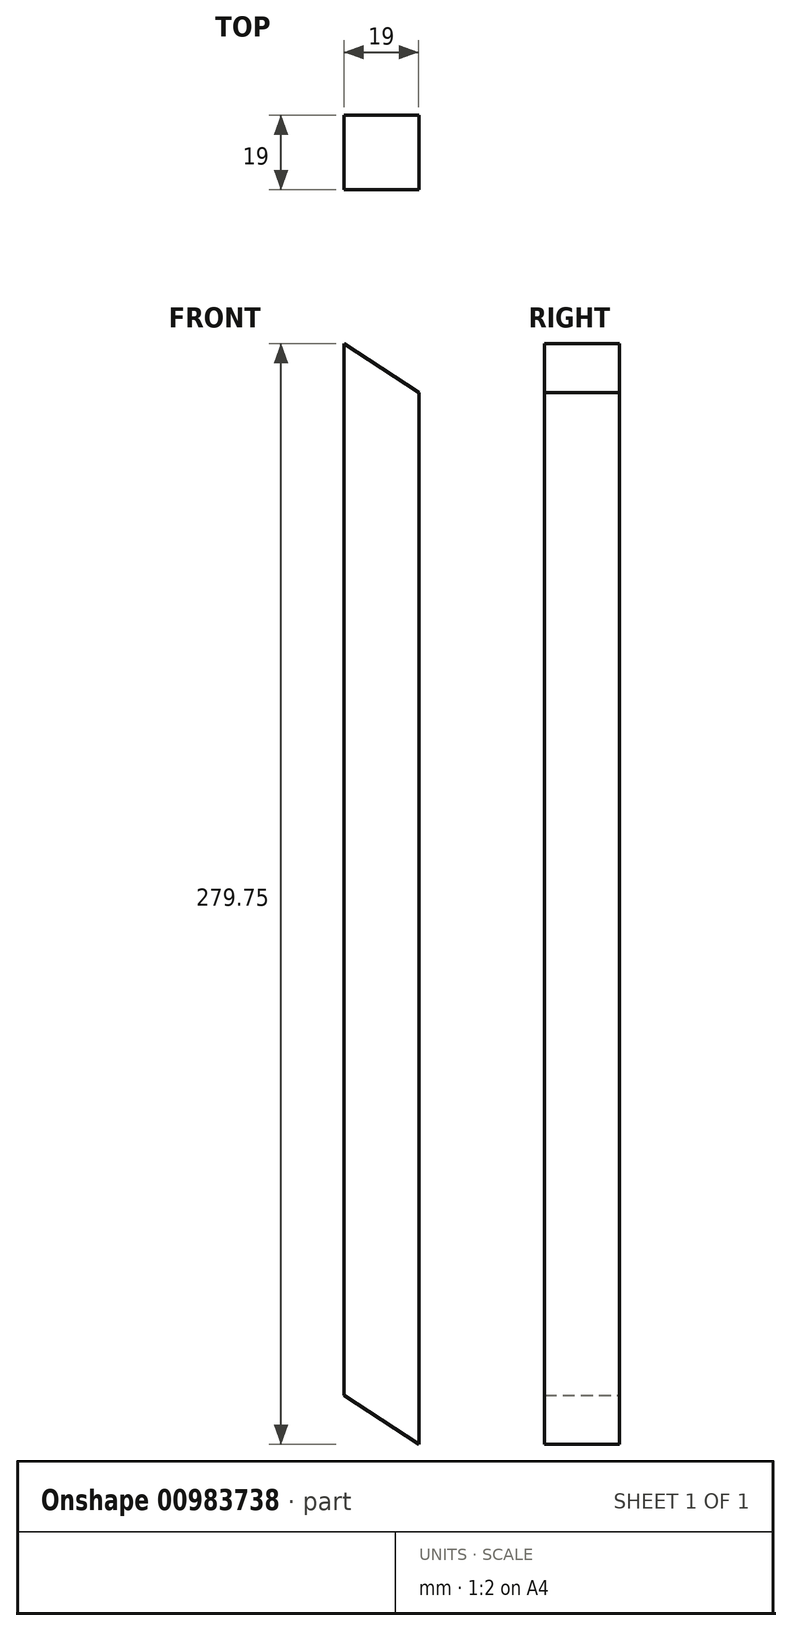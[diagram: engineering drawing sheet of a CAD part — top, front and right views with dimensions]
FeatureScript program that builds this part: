
annotation { "Feature Type Name" : "Feature", "Feature Type Description" : "" }
export const myFeature = defineFeature(function(context is Context, id is Id, definition is map)
    precondition{}
    {
        {
            var Q0;
            Q0=qCreatedBy(makeId("Front.planeOp"),FACE);
            var sketch = newSketch(context, id + "F0", { "sketchPlane" : qUnion([Q0])});
            skLineSegment(sketch, "E0.top", {"start": v(-7.49, -229.51) * mm, "end": v(11.51, -229.51) * mm});
            skLineSegment(sketch, "E0.left", {"start": v(-7.49, 50.49) * mm, "end": v(-7.49, -216.73) * mm});
            skLineSegment(sketch, "E0.right", {"start": v(11.51, 37.96) * mm, "end": v(11.51, -229.51) * mm});
            skLineSegment(sketch, "E1", {"start": v(-7.49, 50.49) * mm, "end": v(11.51, 37.96) * mm});
            skLineSegment(sketch, "E2", {"start": v(-7.49, -216.73) * mm, "end": v(11.51, -229.26) * mm});
            skSolve(sketch);
        }
        {
            var Q0;
            Q0=makeQuery(id+"F0.imprint","IMPRINT",FACE,{"disambiguationData":[TD([[makeQuery(id+"F0.imprint","IMPRINT",EDGE,{"derivedFrom":sQuery(id+"F0.wireOp",EDGE,"E0.left")}),1.0]])]});
            extrude(context, id + "F1", {"entities" : qUnion([Q0]), "depth" : 19 * mm, "offsetDistance" : 25.4 * mm});
        }
        {
            var Q0;
            Q0=makeQuery(id+"F1.opExtrude","SWEPT_BODY",BODY,{"disambiguationData":[OSD([sQuery(id+"F0.wireOp",EDGE,"E0.left"),sQuery(id+"F0.wireOp",EDGE,"E0.right"),sQuery(id+"F0.wireOp",EDGE,"E1"),sQuery(id+"F0.wireOp",EDGE,"E2")])]});
            transform(context, id + "F2", {"entities" : qUnion([Q0]), "transformType" : TransformType.TRANSLATION_3D, "dx" : 0 * mm, "dy" : 0 * mm, "dz" : 0 * mm, "makeCopy" : true});
        }
        {
            var Q0;
            Q0=makeQuery(id+"F2.opPattern","COPY",BODY,{"derivedFrom":makeQuery(id+"F1.opExtrude","SWEPT_BODY",BODY,{"disambiguationData":[OSD([sQuery(id+"F0.wireOp",EDGE,"E0.left"),sQuery(id+"F0.wireOp",EDGE,"E0.right"),sQuery(id+"F0.wireOp",EDGE,"E1"),sQuery(id+"F0.wireOp",EDGE,"E2")])]}),"instanceName":"1"});
            deleteBodies(context, id + "F3", {"entities" : qUnion([Q0])});
        }
    });
